# Revit family: NBS_Senator_DmstcChrs_Lyft
name_source: partatom
category: Furniture
revit_build: Autodesk Revit 2018 (Build: 20190510_1515(x64)
units: mm (PartAtom-declared; Revit-internal decimal feet)

## family parameters
Always vertical = Yes
Cut with Voids When Loaded = No
Room Calculation Point = No
Shared = No
Work Plane-Based = No

## types (1)
- LYF01
    Application = Office and educational settings
    AssetType = Fixed
    BIMObjectName = NBS_Senator_DomesticChairs_Lyft_LYF01
    BaseDepth = 340 mm  [stored 1.11549 ft]
    BodyMaterial = NBS_Senator_Plastic_White
    BottomSeatMaterial = NBS_Senator_Plastic_White
    Category = Pr_40_50_12_22:Dining chairs
    Color = Black, graphite, light grey
    Description = Stool
    DurationUnit = year
    ExpectedLife = 10
    Features = Soft touch seat, height adjustment lever
    Finish = Plastic
    HighestSeatingHeight = 805 mm  [stored 2.64108 ft]
    IfcExportAs = IfcFurnitureType
    IfcExportType = CHAIR
    IsBuiltIn = No
    LegAdjustementMaterial = NBS_Senator_Plastic_Black
    LegMaterial = NBS_Senator_Plastic_White
    LowestSeatingHeight = 535 mm  [stored 1.75525 ft]
    ManufacturerName = The Senator Group
    ManufacturerURL = www.senator.co.uk
    Material = Polyphropylene, PU foam, steel
    MaximumHeight = 805 mm  [stored 2.64108 ft]
    MinimumHeight = 535 mm  [stored 1.75525 ft]
    ModelNumber = LYF01
    ModelReference = Lyft_LYF01
    NBSCertification = www.nationalbimlibrary.com/cert/fgmpih0s
    NBSDescription = Domestic chairs
    NBSReference = 45-35-20/365
    Name = DomesticChairs_Lyft_LYF01_Senator
    NominalDepth = 155 mm  [stored 0.50853 ft]
    NominalHeight = 805 mm  [stored 2.64108 ft]
    NominalLength = 0 mm  [stored 0 ft]
    NominalWidth = 360 mm  [stored 1.1811 ft]
    OptionalExtras = Choice of finish options available, Gas Cylinder to match plastic colour
    ProductInformation = http://www.thesenatorgroup.com
    SeatDepth = 155 mm  [stored 0.50853 ft]
    SeatHeight = 535 mm  [stored 1.75525 ft]
    SeatWidth = 360 mm  [stored 1.1811 ft]
    SeatingHeight = 0 mm  [stored 0 ft]
    Size = 155 x 805 x 360 mm
    SoftTouchBaseMaterial = NBS_Senator_Plastic_Black
    SoftTouchPUSeatMaterial = NBS_Senator_Plastic_Black
    SpecifiableFeatures = Structural moulded body with integral, height adjustment lever, Soft touch PU moulded base, Soft touch PU moulded seat
    Status = UNSET
    Style = Stool
    SustainabilityPerformance = 100% recyclable
    Uniclass2015Code = Pr_40_50_12_22
    Uniclass2015Title = Dining chairs
    Uniclass2015Version = Products v1.16
    Version = 1
    WarrantyDescription = Senator warrants that its manufactured products are free from manufacturing defects - in materials or workmanship - for a period of ten (10) years on Senator Seating ranges; and fifteen (15) years on Senator Desking ranges - exceptions are listed below. Senator will repair or replace (at Senator’s sole discretion) with comparable free of charge materials / components, any product / component, which fails under normal use in a single shift environment, as a result of a defect in the materials and / or workmanship
    WarrantyDurationParts = 10
    WarrantyDurationUnit = year
    Weight = 5 kg

note: [stored X ft] marks values corroborated as IEEE doubles in the binary element streams (Revit-internal decimal feet)

## geometry (parser evidence)
native form markers: Sweep x2
no freeform markers — native parametric forms only
